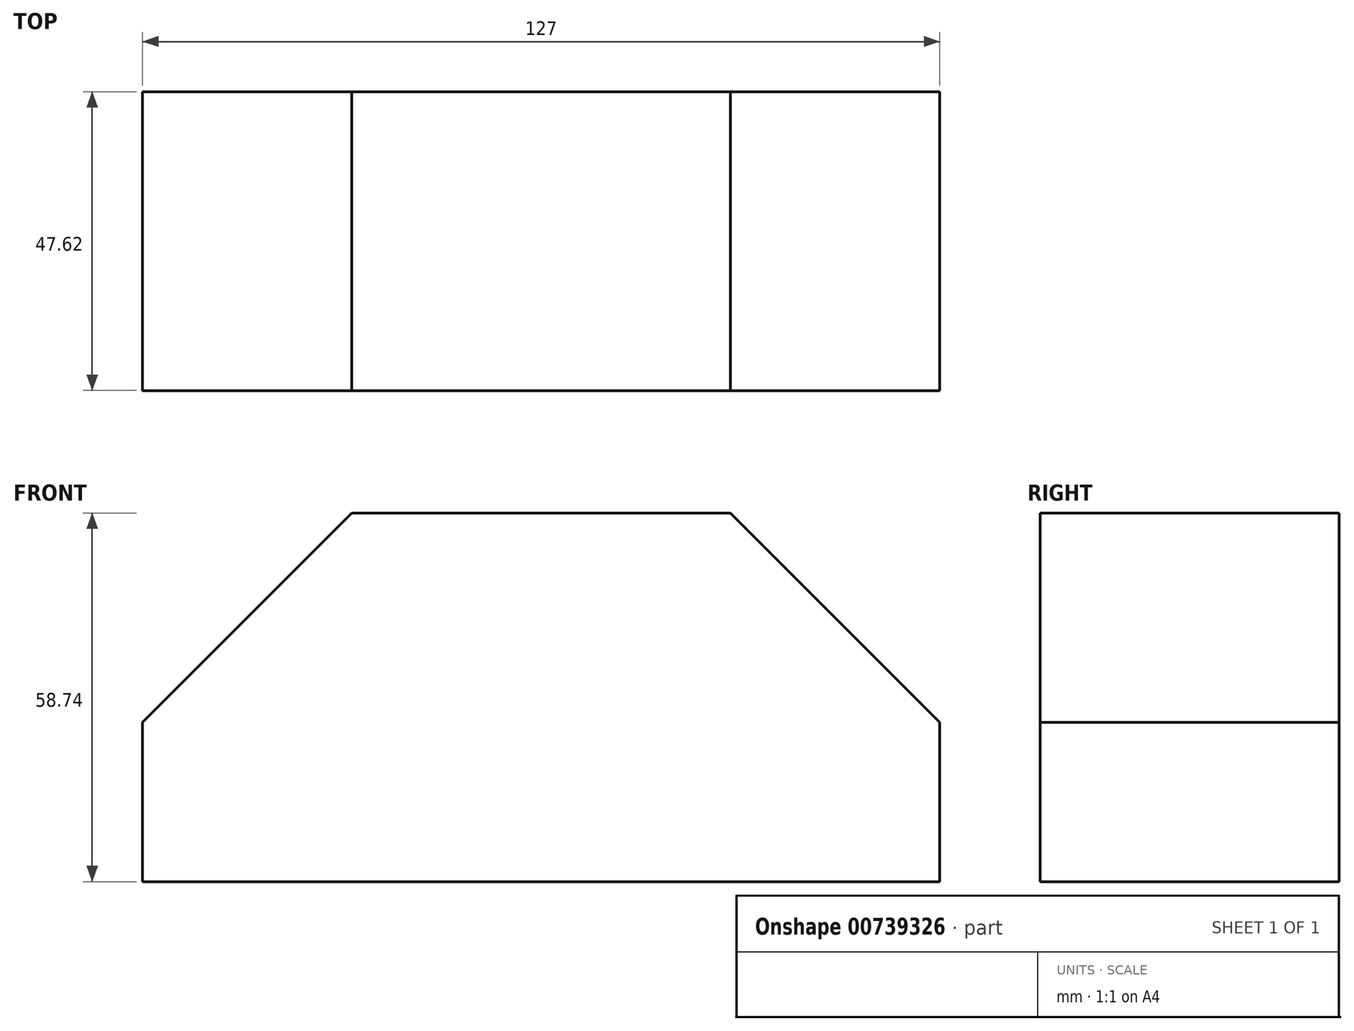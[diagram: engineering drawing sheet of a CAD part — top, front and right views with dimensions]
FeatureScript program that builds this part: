
annotation { "Feature Type Name" : "Feature", "Feature Type Description" : "" }
export const myFeature = defineFeature(function(context is Context, id is Id, definition is map)
    precondition{}
    {
        {
            var Q0;
            Q0=qCreatedBy(makeId("Front.planeOp"),FACE);
            var sketch = newSketch(context, id + "F0", { "sketchPlane" : qUnion([Q0])});
            skLineSegment(sketch, "E0", {"start": v(-62.34, -25.4) * mm, "end": v(64.66, -25.4) * mm});
            skLineSegment(sketch, "E1", {"start": v(64.66, 0) * mm, "end": v(64.66, -25.4) * mm});
            skLineSegment(sketch, "E2", {"start": v(-62.34, -25.4) * mm, "end": v(-62.34, 0) * mm});
            skLineSegment(sketch, "E3", {"start": v(-62.34, 0) * mm, "end": v(-29, 33.34) * mm});
            skLineSegment(sketch, "E4", {"start": v(-29, 33.34) * mm, "end": v(31.32, 33.34) * mm});
            skLineSegment(sketch, "E5", {"start": v(31.32, 33.34) * mm, "end": v(64.66, 0) * mm});
            skSolve(sketch);
        }
        {
            var Q0;
            Q0 = qSketchRegion(id + "F0", true);
            extrude(context, id + "F1", {"entities" : qUnion([Q0]), "depth" : 47.62 * mm, "offsetDistance" : 25.4 * mm});
        }
    });
